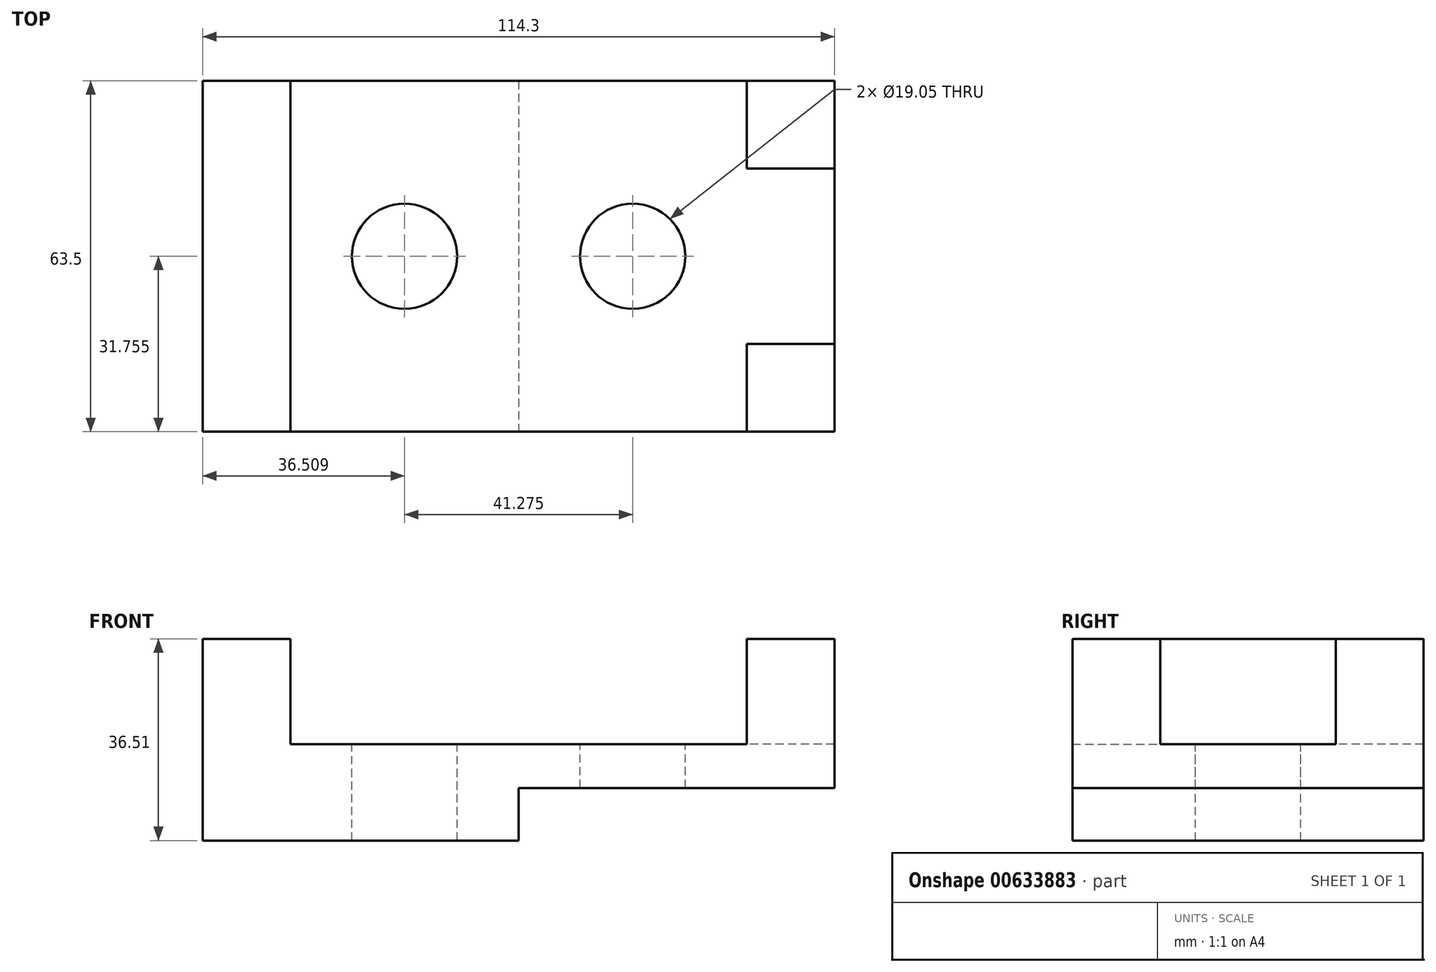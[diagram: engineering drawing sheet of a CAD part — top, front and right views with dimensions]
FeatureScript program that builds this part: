
annotation { "Feature Type Name" : "Feature", "Feature Type Description" : "" }
export const myFeature = defineFeature(function(context is Context, id is Id, definition is map)
    precondition{}
    {
        {
            var Q0;
            Q0=qCreatedBy(makeId("Top.planeOp"),FACE);
            var sketch = newSketch(context, id + "F0", { "sketchPlane" : qUnion([Q0])});
            skLineSegment(sketch, "E0.bottom", {"start": v(-59.3, 14.76) * mm, "end": v(55, 14.76) * mm});
            skLineSegment(sketch, "E0.top", {"start": v(-59.3, -48.74) * mm, "end": v(55, -48.74) * mm});
            skLineSegment(sketch, "E0.left", {"start": v(-59.3, 14.76) * mm, "end": v(-59.3, -48.74) * mm});
            skLineSegment(sketch, "E0.right", {"start": v(55, 14.76) * mm, "end": v(55, -48.74) * mm});
            skSolve(sketch);
        }
        {
            var Q0;
            Q0=makeQuery(id+"F0.imprint","IMPRINT",FACE,{"disambiguationData":[TD([[makeQuery(id+"F0.imprint","IMPRINT",EDGE,{"derivedFrom":sQuery(id+"F0.wireOp",EDGE,"E0.bottom")}),-1.0]])]});
            extrude(context, id + "F1", {"entities" : qUnion([Q0]), "depth" : 36.5 * mm, "offsetDistance" : 25.4 * mm});
        }
        {
            var Q0;
            Q0=makeQuery(id+"F1.opExtrude","SWEPT_FACE",FACE,{"disambiguationData":[OSD([sQuery(id+"F0.wireOp",EDGE,"E0.top")])]});
            var sketch = newSketch(context, id + "F2", { "sketchPlane" : qUnion([Q0])});
            skLineSegment(sketch, "E1.bottom", {"start": v(55, 0) * mm, "end": v(-2.14, 0) * mm});
            skLineSegment(sketch, "E1.top", {"start": v(55, 9.53) * mm, "end": v(-2.14, 9.53) * mm});
            skLineSegment(sketch, "E1.left", {"start": v(55, 0) * mm, "end": v(55, 9.53) * mm});
            skLineSegment(sketch, "E1.right", {"start": v(-2.14, 0) * mm, "end": v(-2.14, 9.52) * mm});
            skSolve(sketch);
        }
        {
            var Q0;
            Q0=makeQuery(id+"F2.imprint","IMPRINT",FACE,{"disambiguationData":[TD([[makeQuery(id+"F2.imprint","IMPRINT",EDGE,{"derivedFrom":sQuery(id+"F2.wireOp",EDGE,"E1.bottom")}),1.0]])]});
            extrude(context, id + "F3", {"entities" : qUnion([Q0]), "operationType" : NewBodyOperationType.REMOVE, "endBound" : BoundingType.THROUGH_ALL, "oppositeDirection" : true, "depth" : 25.4 * mm, "offsetDistance" : 25.4 * mm});
        }
        {
            var Q0;
            Q0=makeQuery(id+"F1.opExtrude","CAP_FACE",FACE,{"disambiguationData":[OSD([sQuery(id+"F0.wireOp",EDGE,"E0.bottom"),sQuery(id+"F0.wireOp",EDGE,"E0.top"),sQuery(id+"F0.wireOp",EDGE,"E0.left"),sQuery(id+"F0.wireOp",EDGE,"E0.right")])],"isStart":false});
            var sketch = newSketch(context, id + "F4", { "sketchPlane" : qUnion([Q0])});
            skLineSegment(sketch, "E2.bottom", {"start": v(55, 14.76) * mm, "end": v(-43.42, 14.76) * mm});
            skLineSegment(sketch, "E2.top", {"start": v(55, -48.74) * mm, "end": v(-43.42, -48.74) * mm});
            skLineSegment(sketch, "E2.left", {"start": v(55, 14.76) * mm, "end": v(55, -48.74) * mm});
            skLineSegment(sketch, "E2.right", {"start": v(-43.42, 14.76) * mm, "end": v(-43.42, -48.74) * mm});
            skSolve(sketch);
        }
        {
            var Q0;
            Q0=makeQuery(id+"F4.imprint","IMPRINT",FACE,{"disambiguationData":[TD([[makeQuery(id+"F4.imprint","IMPRINT",EDGE,{"derivedFrom":sQuery(id+"F4.wireOp",EDGE,"E2.bottom")}),-1.0]])]});
            extrude(context, id + "F5", {"entities" : qUnion([Q0]), "operationType" : NewBodyOperationType.REMOVE, "oppositeDirection" : true, "depth" : 19.05 * mm, "offsetDistance" : 25.4 * mm});
        }
        {
            var Q0;
            Q0=makeQuery(id+"F5.boolean.opBoolean","COPY",FACE,{"derivedFrom":makeQuery(id+"F5.opExtrude","CAP_FACE",FACE,{"disambiguationData":[OSD([sQuery(id+"F4.wireOp",EDGE,"E2.bottom"),sQuery(id+"F4.wireOp",EDGE,"E2.top"),sQuery(id+"F4.wireOp",EDGE,"E2.left"),sQuery(id+"F4.wireOp",EDGE,"E2.right")])],"isStart":false})});
            var sketch = newSketch(context, id + "F6", { "sketchPlane" : qUnion([Q0])});
            skLineSegment(sketch, "E3.bottom", {"start": v(55, 14.76) * mm, "end": v(39.13, 14.76) * mm});
            skLineSegment(sketch, "E3.top", {"start": v(55, -1.11) * mm, "end": v(39.13, -1.11) * mm});
            skLineSegment(sketch, "E3.left", {"start": v(55, 14.76) * mm, "end": v(55, -1.11) * mm});
            skLineSegment(sketch, "E3.right", {"start": v(39.13, 14.76) * mm, "end": v(39.13, -1.11) * mm});
            skLineSegment(sketch, "E4.bottom", {"start": v(55, -48.74) * mm, "end": v(39.13, -48.74) * mm});
            skLineSegment(sketch, "E4.top", {"start": v(55, -32.86) * mm, "end": v(39.13, -32.86) * mm});
            skLineSegment(sketch, "E4.left", {"start": v(55, -48.74) * mm, "end": v(55, -32.86) * mm});
            skLineSegment(sketch, "E4.right", {"start": v(39.13, -48.74) * mm, "end": v(39.13, -32.86) * mm});
            skSolve(sketch);
        }
        {
            var Q0;
            Q0=makeQuery(id+"F6.imprint","IMPRINT",FACE,{"disambiguationData":[TD([[makeQuery(id+"F6.imprint","IMPRINT",EDGE,{"derivedFrom":sQuery(id+"F6.wireOp",EDGE,"E3.bottom")}),-1.0]])]});
            var Q1;
            Q1=makeQuery(id+"F6.imprint","IMPRINT",FACE,{"disambiguationData":[TD([[makeQuery(id+"F6.imprint","IMPRINT",EDGE,{"derivedFrom":sQuery(id+"F6.wireOp",EDGE,"E4.bottom")}),1.0]])]});
            extrude(context, id + "F7", {"entities" : qUnion([Q0, Q1]), "operationType" : NewBodyOperationType.ADD, "depth" : 19.05 * mm, "offsetDistance" : 25.4 * mm});
        }
        {
            var Q0;
            Q0=makeQuery(id+"F5.boolean.opBoolean","COPY",FACE,{"derivedFrom":makeQuery(id+"F5.opExtrude","CAP_FACE",FACE,{"disambiguationData":[OSD([sQuery(id+"F4.wireOp",EDGE,"E2.bottom"),sQuery(id+"F4.wireOp",EDGE,"E2.top"),sQuery(id+"F4.wireOp",EDGE,"E2.left"),sQuery(id+"F4.wireOp",EDGE,"E2.right")])],"isStart":false})});
            var sketch = newSketch(context, id + "F8", { "sketchPlane" : qUnion([Q0])});
            skCircle(sketch, "E5", {"center": v(18.5, -16.99) * mm, "radius": 9.53 * mm});
            skPoint(sketch, "E5.centerSnap0", {"position": v(55, -16.99) * mm});
            skCircle(sketch, "E6", {"center": v(-22.78, -16.99) * mm, "radius": 9.53 * mm});
            skSolve(sketch);
        }
        {
            var Q0;
            Q0=makeQuery(id+"F8.imprint","IMPRINT",FACE,{"disambiguationData":[TD([[makeQuery(id+"F8.imprint","IMPRINT",EDGE,{"derivedFrom":sQuery(id+"F8.wireOp",EDGE,"E6")}),1.0]])]});
            var Q1;
            Q1=makeQuery(id+"F8.imprint","IMPRINT",FACE,{"disambiguationData":[TD([[makeQuery(id+"F8.imprint","IMPRINT",EDGE,{"derivedFrom":sQuery(id+"F8.wireOp",EDGE,"E5")}),1.0]])]});
            extrude(context, id + "F9", {"entities" : qUnion([Q0, Q1]), "operationType" : NewBodyOperationType.REMOVE, "endBound" : BoundingType.THROUGH_ALL, "oppositeDirection" : true, "depth" : 25.4 * mm, "offsetDistance" : 25.4 * mm});
        }
    });
